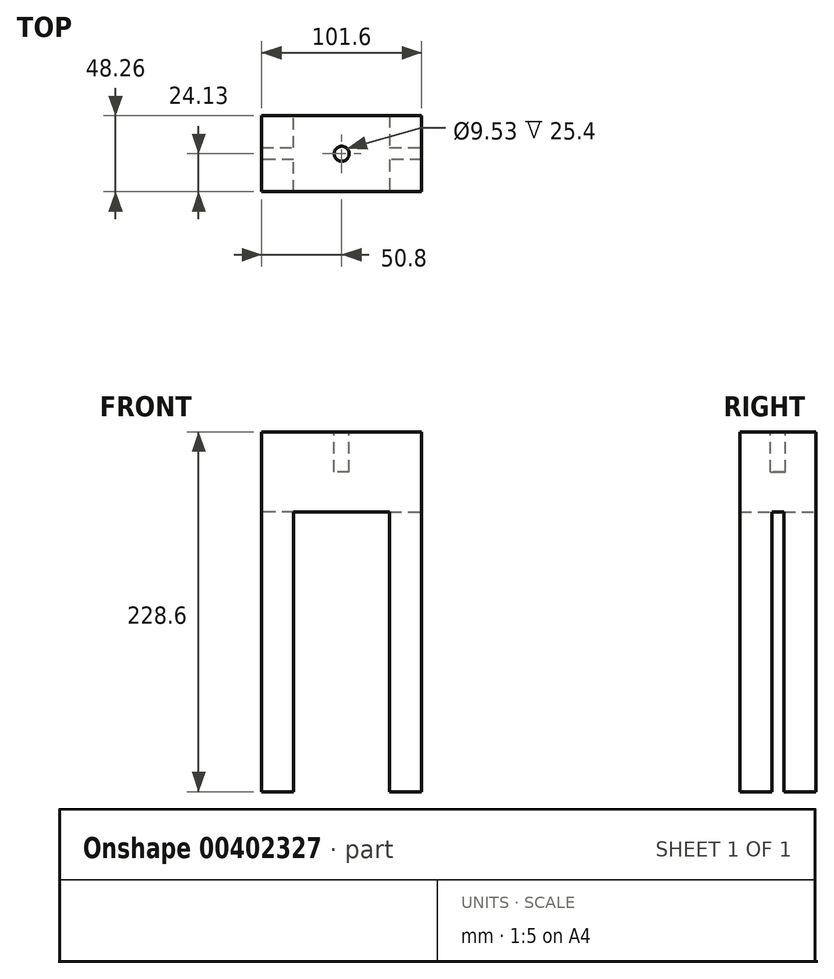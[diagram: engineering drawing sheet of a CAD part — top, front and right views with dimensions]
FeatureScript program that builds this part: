
annotation { "Feature Type Name" : "Feature", "Feature Type Description" : "" }
export const myFeature = defineFeature(function(context is Context, id is Id, definition is map)
    precondition{}
    {
        {
            var Q0;
            Q0=qCreatedBy(makeId("Top.planeOp"),FACE);
            var sketch = newSketch(context, id + "F0", { "sketchPlane" : qUnion([Q0])});
            skLineSegment(sketch, "E0.bottom", {"start": v(-50.8, 24.13) * mm, "end": v(50.8, 24.13) * mm});
            skLineSegment(sketch, "E0.top", {"start": v(-50.8, -24.13) * mm, "end": v(50.8, -24.13) * mm});
            skLineSegment(sketch, "E0.left", {"start": v(-50.8, 24.13) * mm, "end": v(-50.8, -24.13) * mm});
            skLineSegment(sketch, "E0.right", {"start": v(50.8, 24.13) * mm, "end": v(50.8, -24.13) * mm});
            skPoint(sketch, "E0.middle", {"position": v(0, 0) * mm});
            skSolve(sketch);
        }
        {
            var Q0;
            Q0 = qSketchRegion(id + "F0", true);
            extrude(context, id + "F1", {"entities" : qUnion([Q0]), "depth" : 228.6 * mm, "offsetDistance" : 25.4 * mm, "symmetric" : true});
        }
        {
            var Q0;
            Q0=makeQuery(id+"F1.opExtrude","CAP_FACE",FACE,{"disambiguationData":[OSD([sQuery(id+"F0.wireOp",EDGE,"E0.bottom"),sQuery(id+"F0.wireOp",EDGE,"E0.top"),sQuery(id+"F0.wireOp",EDGE,"E0.left"),sQuery(id+"F0.wireOp",EDGE,"E0.right")])],"isStart":true});
            var sketch = newSketch(context, id + "F2", { "sketchPlane" : qUnion([Q0])});
            skLineSegment(sketch, "E1", {"start": v(-30.48, 24.13) * mm, "end": v(-30.48, 3.81) * mm});
            skLineSegment(sketch, "E2", {"start": v(-30.48, 3.81) * mm, "end": v(-50.8, 3.81) * mm});
            skLineSegment(sketch, "E3", {"start": v(-50.8, 3.81) * mm, "end": v(-50.8, -3.81) * mm});
            skLineSegment(sketch, "E4", {"start": v(-50.8, -3.81) * mm, "end": v(-30.48, -3.81) * mm});
            skLineSegment(sketch, "E5", {"start": v(-30.48, -3.81) * mm, "end": v(-30.48, -24.13) * mm});
            skLineSegment(sketch, "E6", {"start": v(-30.48, -24.13) * mm, "end": v(30.48, -24.13) * mm});
            skLineSegment(sketch, "E7", {"start": v(30.48, -24.13) * mm, "end": v(30.48, -3.81) * mm});
            skLineSegment(sketch, "E8", {"start": v(30.48, -3.8) * mm, "end": v(50.8, -3.8) * mm});
            skLineSegment(sketch, "E9", {"start": v(50.8, -3.8) * mm, "end": v(50.8, 3.8) * mm});
            skLineSegment(sketch, "E10", {"start": v(50.8, 3.81) * mm, "end": v(30.48, 3.81) * mm});
            skLineSegment(sketch, "E11", {"start": v(30.48, 3.81) * mm, "end": v(30.48, 24.13) * mm});
            skLineSegment(sketch, "E12", {"start": v(30.48, 24.13) * mm, "end": v(-30.48, 24.13) * mm});
            skSolve(sketch);
        }
        {
            var Q0;
            Q0 = qSketchRegion(id + "F2", true);
            extrude(context, id + "F3", {"entities" : qUnion([Q0]), "operationType" : NewBodyOperationType.REMOVE, "oppositeDirection" : true, "depth" : 177.8 * mm, "offsetDistance" : 25.4 * mm});
        }
        {
            var Q0;
            Q0=makeQuery(id+"F1.opExtrude","CAP_FACE",FACE,{"disambiguationData":[OSD([sQuery(id+"F0.wireOp",EDGE,"E0.bottom"),sQuery(id+"F0.wireOp",EDGE,"E0.top"),sQuery(id+"F0.wireOp",EDGE,"E0.left"),sQuery(id+"F0.wireOp",EDGE,"E0.right")])],"isStart":false});
            var sketch = newSketch(context, id + "F4", { "sketchPlane" : qUnion([Q0])});
            skCircle(sketch, "E13", {"center": v(0, 0) * mm, "radius": 4.76 * mm});
            skSolve(sketch);
        }
        {
            var Q0;
            Q0 = qSketchRegion(id + "F4", true);
            extrude(context, id + "F5", {"entities" : qUnion([Q0]), "operationType" : NewBodyOperationType.REMOVE, "oppositeDirection" : true, "depth" : 25.4 * mm});
        }
    });
